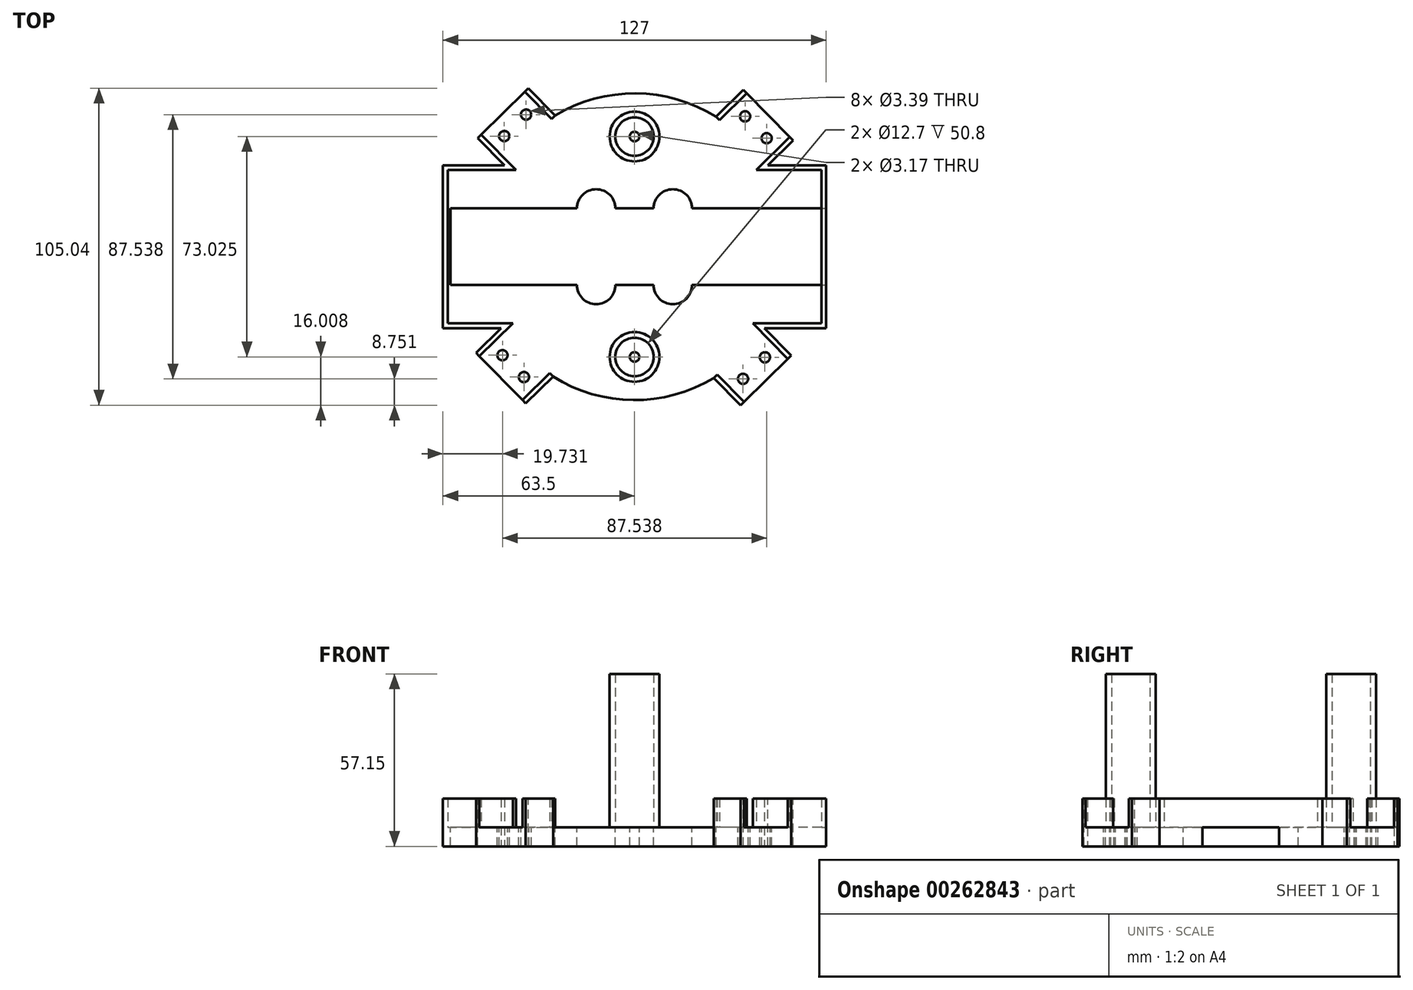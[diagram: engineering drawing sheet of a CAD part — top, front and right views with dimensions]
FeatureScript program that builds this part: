
annotation { "Feature Type Name" : "Feature", "Feature Type Description" : "" }
export const myFeature = defineFeature(function(context is Context, id is Id, definition is map)
    precondition{}
    {
        {
            var Q0;
            Q0=qCreatedBy(makeId("Top.planeOp"),FACE);
            var sketch = newSketch(context, id + "F0", { "sketchPlane" : qUnion([Q0])});
            skCircle(sketch, "E0", {"center": v(0, 0) * mm, "radius": 50.8 * mm});
            skSolve(sketch);
        }
        {
            var Q0;
            Q0=qSketchRegion(id+"F0",true);
            extrude(context, id + "F1", {"entities" : qUnion([Q0]), "depth" : 6.35 * mm});
        }
        {
            var Q0;
            Q0=makeQuery(id+"F1.opExtrude","CAP_FACE",FACE,{"disambiguationData":[OSD([sQuery(id+"F0.wireOp",EDGE,"E0")])],"isStart":false});
            var sketch = newSketch(context, id + "F2", { "sketchPlane" : qUnion([Q0])});
            skLineSegment(sketch, "E1.bottom", {"start": v(63.5, 26.99) * mm, "end": v(-63.5, 26.99) * mm});
            skLineSegment(sketch, "E1.top", {"start": v(63.5, -26.99) * mm, "end": v(-63.5, -26.99) * mm});
            skLineSegment(sketch, "E1.left", {"start": v(63.5, 26.99) * mm, "end": v(63.5, -26.99) * mm});
            skLineSegment(sketch, "E1.right", {"start": v(-63.5, 26.99) * mm, "end": v(-63.5, -26.99) * mm});
            skPoint(sketch, "E1.middle", {"position": v(0, 0) * mm});
            skSolve(sketch);
        }
        {
            var Q0;
            Q0=qSketchRegion(id+"F2",true);
            extrude(context, id + "F3", {"entities" : qUnion([Q0]), "operationType" : NewBodyOperationType.ADD, "oppositeDirection" : true, "depth" : 6.35 * mm});
        }
        {
            var Q0;
            Q0=makeQuery(id+"F3.boolean.opBoolean","MERGE",FACE,{"derivedFrom":[makeQuery(id+"F1.opExtrude","CAP_FACE",FACE,{"disambiguationData":[OSD([sQuery(id+"F0.wireOp",EDGE,"E0")])],"isStart":false}),makeQuery(id+"F3.opExtrude","CAP_FACE",FACE,{"disambiguationData":[OSD([sQuery(id+"F2.wireOp",EDGE,"E1.bottom"),sQuery(id+"F2.wireOp",EDGE,"E1.top"),sQuery(id+"F2.wireOp",EDGE,"E1.left"),sQuery(id+"F2.wireOp",EDGE,"E1.right")])],"isStart":true})]});
            var sketch = newSketch(context, id + "F4", { "sketchPlane" : qUnion([Q0])});
            skPoint(sketch, "E2", {"position": v(0, 26.99) * mm});
            skPoint(sketch, "E3", {"position": v(0, -26.99) * mm});
            skCircle(sketch, "E4", {"center": v(0, 36.51) * mm, "radius": 8.26 * mm});
            skCircle(sketch, "E5", {"center": v(0, -36.51) * mm, "radius": 8.26 * mm});
            skCircle(sketch, "E6", {"center": v(0, 36.51) * mm, "radius": 6.35 * mm});
            skCircle(sketch, "E7", {"center": v(0, -36.51) * mm, "radius": 6.35 * mm});
            skSolve(sketch);
        }
        {
            var Q0;
            Q0=makeQuery(id+"F4.imprint","IMPRINT",FACE,{"disambiguationData":[TD([[makeQuery(id+"F4.imprint","IMPRINT",EDGE,{"derivedFrom":sQuery(id+"F4.wireOp",EDGE,"E5")}),1.0]])]});
            var Q1;
            Q1=makeQuery(id+"F4.imprint","IMPRINT",FACE,{"disambiguationData":[TD([[makeQuery(id+"F4.imprint","IMPRINT",EDGE,{"derivedFrom":sQuery(id+"F4.wireOp",EDGE,"E4")}),1.0]])]});
            extrude(context, id + "F5", {"entities" : qUnion([Q0, Q1]), "operationType" : NewBodyOperationType.ADD, "depth" : 50.8 * mm});
        }
        {
            var Q0;
            {var subQ0=sQuery(id+"F2.wireOp",EDGE,"E1.bottom");var subQ1=sQuery(id+"F0.wireOp",EDGE,"E0");var subQ2=sQuery(id+"F2.wireOp",EDGE,"E1.top");Q0=makeQuery(id+"F5.boolean.opBoolean","SPLIT",FACE,{"disambiguationData":[TD([makeQuery(id+"F1.opExtrude","SWEPT_FACE",FACE,{"disambiguationData":[OSD([subQ1])]})])],"derivedFrom":makeQuery(id+"F3.boolean.opBoolean","MERGE",FACE,{"derivedFrom":[makeQuery(id+"F1.opExtrude","CAP_FACE",FACE,{"disambiguationData":[OSD([subQ1])],"isStart":false}),makeQuery(id+"F3.opExtrude","CAP_FACE",FACE,{"disambiguationData":[OSD([subQ0,subQ2,sQuery(id+"F2.wireOp",EDGE,"E1.left"),sQuery(id+"F2.wireOp",EDGE,"E1.right")])],"isStart":true})]})});}
            var Q1;
            {var subQ0=sQuery(id+"F2.wireOp",EDGE,"E1.bottom");var subQ1=sQuery(id+"F0.wireOp",EDGE,"E0");var subQ2=sQuery(id+"F2.wireOp",EDGE,"E1.top");Q1=makeQuery(id+"F5.boolean.opBoolean","SPLIT",FACE,{"disambiguationData":[TD([makeQuery(id+"F1.opExtrude","SWEPT_FACE",FACE,{"disambiguationData":[OSD([subQ1])]})])],"derivedFrom":makeQuery(id+"F3.boolean.opBoolean","MERGE",FACE,{"derivedFrom":[makeQuery(id+"F1.opExtrude","CAP_FACE",FACE,{"disambiguationData":[OSD([subQ1])],"isStart":false}),makeQuery(id+"F3.opExtrude","CAP_FACE",FACE,{"disambiguationData":[OSD([subQ0,subQ2,sQuery(id+"F2.wireOp",EDGE,"E1.left"),sQuery(id+"F2.wireOp",EDGE,"E1.right")])],"isStart":true})]})});}
            var Q2;
            Q2=qCreatedBy(makeId("Top.planeOp"),FACE);
            var Q3;
            {var subQ0=sQuery(id+"F2.wireOp",EDGE,"E1.bottom");var subQ1=sQuery(id+"F0.wireOp",EDGE,"E0");var subQ2=sQuery(id+"F2.wireOp",EDGE,"E1.top");Q3=makeQuery(id+"F5.boolean.opBoolean","SPLIT",FACE,{"disambiguationData":[TD([makeQuery(id+"F1.opExtrude","SWEPT_FACE",FACE,{"disambiguationData":[OSD([subQ1])]})])],"derivedFrom":makeQuery(id+"F3.boolean.opBoolean","MERGE",FACE,{"derivedFrom":[makeQuery(id+"F1.opExtrude","CAP_FACE",FACE,{"disambiguationData":[OSD([subQ1])],"isStart":false}),makeQuery(id+"F3.opExtrude","CAP_FACE",FACE,{"disambiguationData":[OSD([subQ0,subQ2,sQuery(id+"F2.wireOp",EDGE,"E1.left"),sQuery(id+"F2.wireOp",EDGE,"E1.right")])],"isStart":true})]})});}
            var sketch = newSketch(context, id + "F6", { "sketchPlane" : qUnion([Q0, Q1, Q2, Q3])});
            skLineSegment(sketch, "E8.bottom", {"start": v(60.96, -12.7) * mm, "end": v(-60.96, -12.7) * mm});
            skLineSegment(sketch, "E8.top", {"start": v(60.96, 12.7) * mm, "end": v(-60.96, 12.7) * mm});
            skLineSegment(sketch, "E8.left", {"start": v(60.96, -12.7) * mm, "end": v(60.96, 12.7) * mm});
            skLineSegment(sketch, "E8.right", {"start": v(-60.96, -12.7) * mm, "end": v(-60.96, 12.7) * mm});
            skPoint(sketch, "E8.middle", {"position": v(0, 0) * mm});
            skSolve(sketch);
        }
        {
            var Q0;
            Q0=qSketchRegion(id+"F6",true);
            var Q1;
            Q1=qSketchRegion(id+"F6",true);
            var Q2;
            Q2=qSketchRegion(id+"F6",true);
            var Q3;
            Q3=qSketchRegion(id+"F6",true);
            extrude(context, id + "F7", {"entities" : qUnion([Q0, Q1, Q2, Q3]), "operationType" : NewBodyOperationType.REMOVE, "endBound" : BoundingType.THROUGH_ALL, "oppositeDirection" : true, "depth" : 25.4 * mm});
        }
        {
            var Q0;
            Q0=makeQuery(id+"F5.boolean.opBoolean","SPLIT",FACE,{"disambiguationData":[TD([makeQuery(id+"F5.opExtrude","SWEPT_FACE",FACE,{"disambiguationData":[OSD([sQuery(id+"F4.wireOp",EDGE,"E6")])]})])],"derivedFrom":makeQuery(id+"F3.boolean.opBoolean","MERGE",FACE,{"derivedFrom":[makeQuery(id+"F1.opExtrude","CAP_FACE",FACE,{"disambiguationData":[OSD([sQuery(id+"F0.wireOp",EDGE,"E0")])],"isStart":false}),makeQuery(id+"F3.opExtrude","CAP_FACE",FACE,{"disambiguationData":[OSD([sQuery(id+"F2.wireOp",EDGE,"E1.bottom"),sQuery(id+"F2.wireOp",EDGE,"E1.top"),sQuery(id+"F2.wireOp",EDGE,"E1.left"),sQuery(id+"F2.wireOp",EDGE,"E1.right")])],"isStart":true})]})});
            var sketch = newSketch(context, id + "F8", { "sketchPlane" : qUnion([Q0])});
            skCircle(sketch, "E9", {"center": v(0, 36.51) * mm, "radius": 1.59 * mm});
            skCircle(sketch, "E10", {"center": v(0, -36.51) * mm, "radius": 1.59 * mm});
            skSolve(sketch);
        }
        {
            var Q0;
            Q0=qSketchRegion(id+"F8",true);
            extrude(context, id + "F9", {"entities" : qUnion([Q0]), "operationType" : NewBodyOperationType.REMOVE, "endBound" : BoundingType.UP_TO_NEXT, "oppositeDirection" : true, "depth" : 25.4 * mm});
        }
        {
            var Q0;
            {var subQ0=sQuery(id+"F0.wireOp",EDGE,"E0");var subQ1=sQuery(id+"F2.wireOp",EDGE,"E1.bottom");var subQ2=sQuery(id+"F2.wireOp",EDGE,"E1.top");Q0=makeQuery(id+"F5.boolean.opBoolean","SPLIT",FACE,{"disambiguationData":[TD([makeQuery(id+"F1.opExtrude","SWEPT_FACE",FACE,{"disambiguationData":[OSD([subQ0])]})])],"derivedFrom":makeQuery(id+"F3.boolean.opBoolean","MERGE",FACE,{"derivedFrom":[makeQuery(id+"F1.opExtrude","CAP_FACE",FACE,{"disambiguationData":[OSD([subQ0])],"isStart":false}),makeQuery(id+"F3.opExtrude","CAP_FACE",FACE,{"disambiguationData":[OSD([subQ1,subQ2,sQuery(id+"F2.wireOp",EDGE,"E1.left"),sQuery(id+"F2.wireOp",EDGE,"E1.right")])],"isStart":true})]})});}
            var sketch = newSketch(context, id + "F10", { "sketchPlane" : qUnion([Q0])});
            skLineSegment(sketch, "E11", {"start": v(-43.04, 26.99) * mm, "end": v(-51.95, 36.04) * mm});
            skLineSegment(sketch, "E12", {"start": v(-51.95, 36.04) * mm, "end": v(-35.2, 52.52) * mm});
            skLineSegment(sketch, "E13", {"start": v(-35.2, 52.52) * mm, "end": v(-26.3, 43.47) * mm});
            skArc(sketch, "E14", {"start": v(-26.3, 43.47) * mm, "mid": v(-35.63, 36.2) * mm, "end": v(-43.04, 26.99) * mm});
            skLineSegment(sketch, "E15.1.0", {"start": v(-26.99, -43.04) * mm, "end": v(-36.04, -51.95) * mm});
            skLineSegment(sketch, "E15.1.1", {"start": v(-52.52, -35.2) * mm, "end": v(-43.47, -26.3) * mm});
            skLineSegment(sketch, "E15.1.2", {"start": v(-36.04, -51.95) * mm, "end": v(-52.52, -35.2) * mm});
            skArc(sketch, "E15.1.3", {"start": v(-43.47, -26.3) * mm, "mid": v(-36.2, -35.63) * mm, "end": v(-26.99, -43.04) * mm});
            skLineSegment(sketch, "E15.2.0", {"start": v(43.04, -26.99) * mm, "end": v(51.95, -36.04) * mm});
            skLineSegment(sketch, "E15.2.1", {"start": v(35.2, -52.52) * mm, "end": v(26.3, -43.47) * mm});
            skLineSegment(sketch, "E15.2.2", {"start": v(51.95, -36.04) * mm, "end": v(35.2, -52.52) * mm});
            skArc(sketch, "E15.2.3", {"start": v(26.3, -43.47) * mm, "mid": v(35.63, -36.2) * mm, "end": v(43.04, -26.99) * mm});
            skLineSegment(sketch, "E15.3.0", {"start": v(26.99, 43.04) * mm, "end": v(36.04, 51.95) * mm});
            skLineSegment(sketch, "E15.3.1", {"start": v(52.52, 35.2) * mm, "end": v(43.47, 26.3) * mm});
            skLineSegment(sketch, "E15.3.2", {"start": v(36.04, 51.95) * mm, "end": v(52.52, 35.2) * mm});
            skArc(sketch, "E15.3.3", {"start": v(43.47, 26.3) * mm, "mid": v(36.2, 35.63) * mm, "end": v(26.99, 43.04) * mm});
            skSolve(sketch);
        }
        {
            var Q0;
            Q0 = qSketchRegion(id + "F10", true);
            extrude(context, id + "F11", {"entities" : qUnion([Q0]), "operationType" : NewBodyOperationType.ADD, "oppositeDirection" : true, "depth" : 6.35 * mm});
        }
        {
            var Q0;
            {var subQ0=sQuery(id+"F2.wireOp",EDGE,"E1.left");var subQ1=sQuery(id+"F2.wireOp",EDGE,"E1.top");var subQ2=sQuery(id+"F2.wireOp",EDGE,"E1.bottom");var subQ3=sQuery(id+"F0.wireOp",EDGE,"E0");var subQ4=sQuery(id+"F2.wireOp",EDGE,"E1.right");Q0=makeQuery(id+"F11.boolean.opBoolean","MERGE",FACE,{"derivedFrom":[makeQuery(id+"F5.boolean.opBoolean","SPLIT",FACE,{"disambiguationData":[TD([makeQuery(id+"F1.opExtrude","SWEPT_FACE",FACE,{"disambiguationData":[OSD([subQ3])]})])],"derivedFrom":makeQuery(id+"F3.boolean.opBoolean","MERGE",FACE,{"derivedFrom":[makeQuery(id+"F1.opExtrude","CAP_FACE",FACE,{"disambiguationData":[OSD([subQ3])],"isStart":false}),makeQuery(id+"F3.opExtrude","CAP_FACE",FACE,{"disambiguationData":[OSD([subQ2,subQ1,subQ0,subQ4])],"isStart":true})]})}),makeQuery(id+"F11.opExtrude","CAP_FACE",FACE,{"disambiguationData":[OSD([sQuery(id+"F10.wireOp",EDGE,"E11"),sQuery(id+"F10.wireOp",EDGE,"E12"),sQuery(id+"F10.wireOp",EDGE,"E13"),sQuery(id+"F10.wireOp",EDGE,"E14")])],"isStart":true}),makeQuery(id+"F11.opExtrude","CAP_FACE",FACE,{"disambiguationData":[OSD([sQuery(id+"F10.wireOp",EDGE,"E15.1.0"),sQuery(id+"F10.wireOp",EDGE,"E15.1.1"),sQuery(id+"F10.wireOp",EDGE,"E15.1.2"),sQuery(id+"F10.wireOp",EDGE,"E15.1.3")])],"isStart":true}),makeQuery(id+"F11.opExtrude","CAP_FACE",FACE,{"disambiguationData":[OSD([sQuery(id+"F10.wireOp",EDGE,"E15.2.0"),sQuery(id+"F10.wireOp",EDGE,"E15.2.1"),sQuery(id+"F10.wireOp",EDGE,"E15.2.2"),sQuery(id+"F10.wireOp",EDGE,"E15.2.3")])],"isStart":true}),makeQuery(id+"F11.opExtrude","CAP_FACE",FACE,{"disambiguationData":[OSD([sQuery(id+"F10.wireOp",EDGE,"E15.3.0"),sQuery(id+"F10.wireOp",EDGE,"E15.3.1"),sQuery(id+"F10.wireOp",EDGE,"E15.3.2"),sQuery(id+"F10.wireOp",EDGE,"E15.3.3")])],"isStart":true})]});}
            var sketch = newSketch(context, id + "F12", { "sketchPlane" : qUnion([Q0])});
            skLineSegment(sketch, "E16", {"start": v(-63.5, -26.99) * mm, "end": v(-63.5, 26.99) * mm});
            skLineSegment(sketch, "E17", {"start": v(-63.5, 26.99) * mm, "end": v(-43.04, 26.99) * mm});
            skLineSegment(sketch, "E18", {"start": v(-43.04, 26.99) * mm, "end": v(-51.95, 36.04) * mm});
            skLineSegment(sketch, "E19", {"start": v(-51.95, 36.04) * mm, "end": v(-50.81, 37.15) * mm});
            skLineSegment(sketch, "E20", {"start": v(-50.81, 37.15) * mm, "end": v(-39.25, 25.4) * mm});
            skLineSegment(sketch, "E21", {"start": v(-39.25, 25.4) * mm, "end": v(-61.91, 25.4) * mm});
            skLineSegment(sketch, "E22", {"start": v(-61.91, 25.4) * mm, "end": v(-61.91, -25.4) * mm});
            skLineSegment(sketch, "E23", {"start": v(-51.4, -36.33) * mm, "end": v(-52.52, -35.2) * mm});
            skLineSegment(sketch, "E24", {"start": v(-52.52, -35.2) * mm, "end": v(-44.17, -26.99) * mm});
            skLineSegment(sketch, "E25", {"start": v(-44.17, -26.99) * mm, "end": v(-63.5, -26.99) * mm});
            skPoint(sketch, "E26.end.orphan", {"position": v(-35.2, -25.4) * mm});
            skLineSegment(sketch, "E27", {"start": v(-61.91, -25.4) * mm, "end": v(-40.3, -25.4) * mm});
            skLineSegment(sketch, "E28", {"start": v(-26.3, 43.47) * mm, "end": v(-35.2, 52.52) * mm});
            skLineSegment(sketch, "E29", {"start": v(-35.2, 52.52) * mm, "end": v(-36.33, 51.4) * mm});
            skLineSegment(sketch, "E30", {"start": v(-36.33, 51.4) * mm, "end": v(-27.42, 42.35) * mm});
            skLineSegment(sketch, "E31", {"start": v(-27.42, 42.35) * mm, "end": v(-26.3, 43.47) * mm});
            skLineSegment(sketch, "E32", {"start": v(-36.04, -51.95) * mm, "end": v(-37.15, -50.81) * mm});
            skLineSegment(sketch, "E33", {"start": v(-37.15, -50.81) * mm, "end": v(-28.1, -41.9) * mm});
            skLineSegment(sketch, "E34", {"start": v(-28.1, -41.9) * mm, "end": v(-26.99, -43.04) * mm});
            skLineSegment(sketch, "E35", {"start": v(-26.99, -43.04) * mm, "end": v(-36.04, -51.95) * mm});
            skLineSegment(sketch, "E36", {"start": v(-51.4, -36.33) * mm, "end": v(-40.3, -25.4) * mm});
            skPoint(sketch, "E37.orphan", {"position": v(-39.25, -25.4) * mm});
            skLineSegment(sketch, "E38.1.0", {"start": v(44.17, 26.99) * mm, "end": v(63.5, 26.99) * mm});
            skLineSegment(sketch, "E38.1.1", {"start": v(61.91, 25.4) * mm, "end": v(40.3, 25.4) * mm});
            skLineSegment(sketch, "E38.1.2", {"start": v(63.5, -26.99) * mm, "end": v(43.04, -26.99) * mm});
            skLineSegment(sketch, "E38.1.3", {"start": v(39.25, -25.4) * mm, "end": v(61.91, -25.4) * mm});
            skLineSegment(sketch, "E38.1.4", {"start": v(26.3, -43.47) * mm, "end": v(35.2, -52.52) * mm});
            skLineSegment(sketch, "E38.1.5", {"start": v(51.4, 36.33) * mm, "end": v(40.3, 25.4) * mm});
            skLineSegment(sketch, "E38.1.6", {"start": v(52.52, 35.2) * mm, "end": v(44.17, 26.99) * mm});
            skLineSegment(sketch, "E38.1.7", {"start": v(26.99, 43.04) * mm, "end": v(36.04, 51.95) * mm});
            skPoint(sketch, "E38.1.8", {"position": v(39.25, 25.4) * mm});
            skLineSegment(sketch, "E38.1.9", {"start": v(61.91, -25.4) * mm, "end": v(61.91, 25.4) * mm});
            skLineSegment(sketch, "E38.1.10", {"start": v(37.15, 50.81) * mm, "end": v(28.1, 41.9) * mm});
            skLineSegment(sketch, "E38.1.11", {"start": v(36.33, -51.4) * mm, "end": v(27.42, -42.35) * mm});
            skLineSegment(sketch, "E38.1.12", {"start": v(50.81, -37.15) * mm, "end": v(39.25, -25.4) * mm});
            skPoint(sketch, "E38.1.13", {"position": v(35.2, 25.4) * mm});
            skLineSegment(sketch, "E38.1.14", {"start": v(63.5, 26.99) * mm, "end": v(63.5, -26.99) * mm});
            skLineSegment(sketch, "E38.1.15", {"start": v(43.04, -26.99) * mm, "end": v(51.95, -36.04) * mm});
            skLineSegment(sketch, "E38.1.16", {"start": v(51.95, -36.04) * mm, "end": v(50.81, -37.15) * mm});
            skLineSegment(sketch, "E38.1.17", {"start": v(35.2, -52.52) * mm, "end": v(36.33, -51.4) * mm});
            skLineSegment(sketch, "E38.1.18", {"start": v(51.4, 36.33) * mm, "end": v(52.52, 35.2) * mm});
            skLineSegment(sketch, "E38.1.19", {"start": v(36.04, 51.95) * mm, "end": v(37.15, 50.81) * mm});
            skLineSegment(sketch, "E38.1.20", {"start": v(28.1, 41.9) * mm, "end": v(26.99, 43.04) * mm});
            skLineSegment(sketch, "E38.1.21", {"start": v(27.42, -42.35) * mm, "end": v(26.3, -43.47) * mm});
            skPoint(sketch, "E38.center", {"position": v(0, 0) * mm});
            skSolve(sketch);
        }
        {
            var Q0;
            Q0 = qSketchRegion(id + "F12", true);
            extrude(context, id + "F13", {"entities" : qUnion([Q0]), "operationType" : NewBodyOperationType.ADD, "depth" : 9.52 * mm});
        }
        {
            var Q0;
            {var subQ0=sQuery(id+"F2.wireOp",EDGE,"E1.left");var subQ1=sQuery(id+"F2.wireOp",EDGE,"E1.top");var subQ2=sQuery(id+"F2.wireOp",EDGE,"E1.bottom");var subQ3=sQuery(id+"F0.wireOp",EDGE,"E0");var subQ4=sQuery(id+"F2.wireOp",EDGE,"E1.right");Q0=makeQuery(id+"F11.boolean.opBoolean","MERGE",FACE,{"derivedFrom":[makeQuery(id+"F5.boolean.opBoolean","SPLIT",FACE,{"disambiguationData":[TD([makeQuery(id+"F1.opExtrude","SWEPT_FACE",FACE,{"disambiguationData":[OSD([subQ3])]})])],"derivedFrom":makeQuery(id+"F3.boolean.opBoolean","MERGE",FACE,{"derivedFrom":[makeQuery(id+"F1.opExtrude","CAP_FACE",FACE,{"disambiguationData":[OSD([subQ3])],"isStart":false}),makeQuery(id+"F3.opExtrude","CAP_FACE",FACE,{"disambiguationData":[OSD([subQ2,subQ1,subQ0,subQ4])],"isStart":true})]})}),makeQuery(id+"F11.opExtrude","CAP_FACE",FACE,{"disambiguationData":[OSD([sQuery(id+"F10.wireOp",EDGE,"E11"),sQuery(id+"F10.wireOp",EDGE,"E12"),sQuery(id+"F10.wireOp",EDGE,"E13"),sQuery(id+"F10.wireOp",EDGE,"E14")])],"isStart":true}),makeQuery(id+"F11.opExtrude","CAP_FACE",FACE,{"disambiguationData":[OSD([sQuery(id+"F10.wireOp",EDGE,"E15.1.0"),sQuery(id+"F10.wireOp",EDGE,"E15.1.1"),sQuery(id+"F10.wireOp",EDGE,"E15.1.2"),sQuery(id+"F10.wireOp",EDGE,"E15.1.3")])],"isStart":true}),makeQuery(id+"F11.opExtrude","CAP_FACE",FACE,{"disambiguationData":[OSD([sQuery(id+"F10.wireOp",EDGE,"E15.2.0"),sQuery(id+"F10.wireOp",EDGE,"E15.2.1"),sQuery(id+"F10.wireOp",EDGE,"E15.2.2"),sQuery(id+"F10.wireOp",EDGE,"E15.2.3")])],"isStart":true}),makeQuery(id+"F11.opExtrude","CAP_FACE",FACE,{"disambiguationData":[OSD([sQuery(id+"F10.wireOp",EDGE,"E15.3.0"),sQuery(id+"F10.wireOp",EDGE,"E15.3.1"),sQuery(id+"F10.wireOp",EDGE,"E15.3.2"),sQuery(id+"F10.wireOp",EDGE,"E15.3.3")])],"isStart":true})]});}
            var sketch = newSketch(context, id + "F14", { "sketchPlane" : qUnion([Q0])});
            skPoint(sketch, "E39.center", {"position": v(0, 0) * mm});
            skCircle(sketch, "E40", {"center": v(-35.94, 43.77) * mm, "radius": 1.7 * mm});
            skPoint(sketch, "E40.first.point", {"position": v(-37.13, 44.98) * mm});
            skPoint(sketch, "E40.second.point", {"position": v(-37.13, 42.56) * mm});
            skPoint(sketch, "E40.second.point.positionSnap0", {"position": v(-37.13, 44.98) * mm});
            skPoint(sketch, "E40.third.point", {"position": v(-34.74, 42.58) * mm});
            skPoint(sketch, "E40.third.point.positionSnap0", {"position": v(-37.15, 42.58) * mm});
            skCircle(sketch, "E41", {"center": v(-43.19, 36.64) * mm, "radius": 1.7 * mm});
            skPoint(sketch, "E41.first.point", {"position": v(-44.37, 37.85) * mm});
            skPoint(sketch, "E41.second.point", {"position": v(-44.37, 35.44) * mm});
            skPoint(sketch, "E41.second.point.positionSnap0", {"position": v(-44.37, 37.85) * mm});
            skPoint(sketch, "E41.third.point", {"position": v(-42, 35.44) * mm});
            skCircle(sketch, "E42", {"center": v(36.64, 43.19) * mm, "radius": 1.7 * mm});
            skPoint(sketch, "E42.first.point", {"position": v(35.46, 44.4) * mm});
            skPoint(sketch, "E42.second.point", {"position": v(37.83, 44.4) * mm});
            skPoint(sketch, "E42.second.point.positionSnap0", {"position": v(35.46, 44.4) * mm});
            skPoint(sketch, "E42.third.point", {"position": v(37.83, 41.98) * mm});
            skCircle(sketch, "E43", {"center": v(43.77, 35.94) * mm, "radius": 1.7 * mm});
            skPoint(sketch, "E43.first.point", {"position": v(44.98, 37.13) * mm});
            skPoint(sketch, "E43.second.point", {"position": v(42.56, 37.13) * mm});
            skPoint(sketch, "E43.second.point.positionSnap0", {"position": v(44.98, 37.13) * mm});
            skPoint(sketch, "E43.third.point", {"position": v(42.56, 34.76) * mm});
            skPoint(sketch, "E44.first.point.positionSnap0", {"position": v(45.03, -31.28) * mm});
            skPoint(sketch, "E44.second.point", {"position": v(41.98, -35.46) * mm});
            skPoint(sketch, "E44.second.point.positionSnap0", {"position": v(44.4, -35.46) * mm});
            skPoint(sketch, "E44.third.point", {"position": v(41.98, -37.83) * mm});
            skCircle(sketch, "E45", {"center": v(35.94, -43.77) * mm, "radius": 1.7 * mm});
            skPoint(sketch, "E45.first.point", {"position": v(37.15, -42.58) * mm});
            skPoint(sketch, "E45.second.point", {"position": v(34.74, -42.58) * mm});
            skPoint(sketch, "E45.second.point.positionSnap0", {"position": v(37.15, -42.58) * mm});
            skPoint(sketch, "E45.third.point", {"position": v(34.74, -44.96) * mm});
            skCircle(sketch, "E46", {"center": v(-43.77, -35.94) * mm, "radius": 1.7 * mm});
            skPoint(sketch, "E46.first.point", {"position": v(-42.58, -34.74) * mm});
            skPoint(sketch, "E46.first.point.positionSnap0", {"position": v(-44.96, -34.74) * mm});
            skPoint(sketch, "E46.second.point", {"position": v(-44.96, -34.74) * mm});
            skPoint(sketch, "E46.third.point", {"position": v(-44.96, -37.15) * mm});
            skPoint(sketch, "E46.third.point.positionSnap0", {"position": v(-44.96, -34.74) * mm});
            skCircle(sketch, "E47", {"center": v(-36.64, -43.19) * mm, "radius": 1.7 * mm});
            skPoint(sketch, "E47.first.point", {"position": v(-37.85, -42) * mm});
            skPoint(sketch, "E47.first.point.positionSnap0", {"position": v(-35.44, -42) * mm});
            skPoint(sketch, "E47.second.point", {"position": v(-37.85, -44.37) * mm});
            skPoint(sketch, "E47.third.point", {"position": v(-35.44, -44.37) * mm});
            skPoint(sketch, "E47.third.point.positionSnap0", {"position": v(-37.85, -44.37) * mm});
            skPoint(sketch, "E47.third.point.positionSnap1", {"position": v(-35.44, -42) * mm});
            skCircle(sketch, "E48", {"center": v(43.19, -36.64) * mm, "radius": 1.7 * mm});
            skSolve(sketch);
        }
        {
            var Q0;
            Q0 = qSketchRegion(id + "F14", true);
            extrude(context, id + "F15", {"entities" : qUnion([Q0]), "operationType" : NewBodyOperationType.REMOVE, "oppositeDirection" : true, "depth" : 25.4 * mm});
        }
        {
            var Q0;
            Q0=makeQuery(id+"F13.boolean.opBoolean","MERGE",FACE,{"derivedFrom":[makeQuery(id+"F3.opExtrude","SWEPT_FACE",FACE,{"disambiguationData":[OSD([sQuery(id+"F2.wireOp",EDGE,"E1.left")])]}),makeQuery(id+"F13.opExtrude","SWEPT_FACE",FACE,{"disambiguationData":[OSD([sQuery(id+"F12.wireOp",EDGE,"E38.1.14")])]})]});
            var sketch = newSketch(context, id + "F16", { "sketchPlane" : qUnion([Q0])});
            skLineSegment(sketch, "E49.bottom", {"start": v(-12.7, 0) * mm, "end": v(12.7, 0) * mm});
            skLineSegment(sketch, "E49.top", {"start": v(-12.7, 6.35) * mm, "end": v(12.7, 6.35) * mm});
            skLineSegment(sketch, "E49.left", {"start": v(-12.7, 0) * mm, "end": v(-12.7, 6.35) * mm});
            skLineSegment(sketch, "E49.right", {"start": v(12.7, 0) * mm, "end": v(12.7, 6.35) * mm});
            skSolve(sketch);
        }
        {
            var Q0;
            Q0 = qSketchRegion(id + "F16", true);
            extrude(context, id + "F17", {"entities" : qUnion([Q0]), "operationType" : NewBodyOperationType.REMOVE, "oppositeDirection" : true, "depth" : 25.4 * mm});
        }
        {
            var Q0;
            {var subQ0=sQuery(id+"F2.wireOp",EDGE,"E1.left");var subQ1=sQuery(id+"F2.wireOp",EDGE,"E1.top");var subQ2=sQuery(id+"F2.wireOp",EDGE,"E1.bottom");var subQ3=sQuery(id+"F0.wireOp",EDGE,"E0");var subQ4=sQuery(id+"F2.wireOp",EDGE,"E1.right");Q0=makeQuery(id+"F11.boolean.opBoolean","MERGE",FACE,{"derivedFrom":[makeQuery(id+"F5.boolean.opBoolean","SPLIT",FACE,{"disambiguationData":[TD([makeQuery(id+"F1.opExtrude","SWEPT_FACE",FACE,{"disambiguationData":[OSD([subQ3])]})])],"derivedFrom":makeQuery(id+"F3.boolean.opBoolean","MERGE",FACE,{"derivedFrom":[makeQuery(id+"F1.opExtrude","CAP_FACE",FACE,{"disambiguationData":[OSD([subQ3])],"isStart":false}),makeQuery(id+"F3.opExtrude","CAP_FACE",FACE,{"disambiguationData":[OSD([subQ2,subQ1,subQ0,subQ4])],"isStart":true})]})}),makeQuery(id+"F11.opExtrude","CAP_FACE",FACE,{"disambiguationData":[OSD([sQuery(id+"F10.wireOp",EDGE,"E11"),sQuery(id+"F10.wireOp",EDGE,"E12"),sQuery(id+"F10.wireOp",EDGE,"E13"),sQuery(id+"F10.wireOp",EDGE,"E14")])],"isStart":true}),makeQuery(id+"F11.opExtrude","CAP_FACE",FACE,{"disambiguationData":[OSD([sQuery(id+"F10.wireOp",EDGE,"E15.1.0"),sQuery(id+"F10.wireOp",EDGE,"E15.1.1"),sQuery(id+"F10.wireOp",EDGE,"E15.1.2"),sQuery(id+"F10.wireOp",EDGE,"E15.1.3")])],"isStart":true}),makeQuery(id+"F11.opExtrude","CAP_FACE",FACE,{"disambiguationData":[OSD([sQuery(id+"F10.wireOp",EDGE,"E15.2.0"),sQuery(id+"F10.wireOp",EDGE,"E15.2.1"),sQuery(id+"F10.wireOp",EDGE,"E15.2.2"),sQuery(id+"F10.wireOp",EDGE,"E15.2.3")])],"isStart":true}),makeQuery(id+"F11.opExtrude","CAP_FACE",FACE,{"disambiguationData":[OSD([sQuery(id+"F10.wireOp",EDGE,"E15.3.0"),sQuery(id+"F10.wireOp",EDGE,"E15.3.1"),sQuery(id+"F10.wireOp",EDGE,"E15.3.2"),sQuery(id+"F10.wireOp",EDGE,"E15.3.3")])],"isStart":true})]});}
            var sketch = newSketch(context, id + "F18", { "sketchPlane" : qUnion([Q0])});
            skCircle(sketch, "E50", {"center": v(-12.7, 12.7) * mm, "radius": 6.35 * mm});
            skCircle(sketch, "E51.1.0", {"center": v(-12.7, -12.7) * mm, "radius": 6.35 * mm});
            skCircle(sketch, "E51.2.0", {"center": v(12.7, -12.7) * mm, "radius": 6.35 * mm});
            skPoint(sketch, "E51.center", {"position": v(0, 0) * mm});
            skCircle(sketch, "E52.1.3.0", {"center": v(12.7, 12.7) * mm, "radius": 6.35 * mm});
            skSolve(sketch);
        }
        {
            var Q0;
            Q0 = qSketchRegion(id + "F18", true);
            var Q1;
            Q1=makeQuery(id+"F11.boolean.opBoolean","MERGE",FACE,{"derivedFrom":[makeQuery(id+"F3.boolean.opBoolean","MERGE",FACE,{"derivedFrom":[makeQuery(id+"F1.opExtrude","CAP_FACE",FACE,{"disambiguationData":[OSD([sQuery(id+"F0.wireOp",EDGE,"E0")])],"isStart":true}),makeQuery(id+"F3.opExtrude","CAP_FACE",FACE,{"disambiguationData":[OSD([sQuery(id+"F2.wireOp",EDGE,"E1.bottom"),sQuery(id+"F2.wireOp",EDGE,"E1.top"),sQuery(id+"F2.wireOp",EDGE,"E1.left"),sQuery(id+"F2.wireOp",EDGE,"E1.right")])],"isStart":false})]}),makeQuery(id+"F11.opExtrude","CAP_FACE",FACE,{"disambiguationData":[OSD([sQuery(id+"F10.wireOp",EDGE,"E11"),sQuery(id+"F10.wireOp",EDGE,"E12"),sQuery(id+"F10.wireOp",EDGE,"E13"),sQuery(id+"F10.wireOp",EDGE,"E14")])],"isStart":false}),makeQuery(id+"F11.opExtrude","CAP_FACE",FACE,{"disambiguationData":[OSD([sQuery(id+"F10.wireOp",EDGE,"E15.1.0"),sQuery(id+"F10.wireOp",EDGE,"E15.1.1"),sQuery(id+"F10.wireOp",EDGE,"E15.1.2"),sQuery(id+"F10.wireOp",EDGE,"E15.1.3")])],"isStart":false}),makeQuery(id+"F11.opExtrude","CAP_FACE",FACE,{"disambiguationData":[OSD([sQuery(id+"F10.wireOp",EDGE,"E15.2.0"),sQuery(id+"F10.wireOp",EDGE,"E15.2.1"),sQuery(id+"F10.wireOp",EDGE,"E15.2.2"),sQuery(id+"F10.wireOp",EDGE,"E15.2.3")])],"isStart":false}),makeQuery(id+"F11.opExtrude","CAP_FACE",FACE,{"disambiguationData":[OSD([sQuery(id+"F10.wireOp",EDGE,"E15.3.0"),sQuery(id+"F10.wireOp",EDGE,"E15.3.1"),sQuery(id+"F10.wireOp",EDGE,"E15.3.2"),sQuery(id+"F10.wireOp",EDGE,"E15.3.3")])],"isStart":false})]});
            extrude(context, id + "F19", {"entities" : qUnion([Q0]), "operationType" : NewBodyOperationType.REMOVE, "endBound" : BoundingType.UP_TO_SURFACE, "oppositeDirection" : true, "endBoundEntityFace" : qUnion([Q1]), "depth" : 25.4 * mm});
        }
    });
